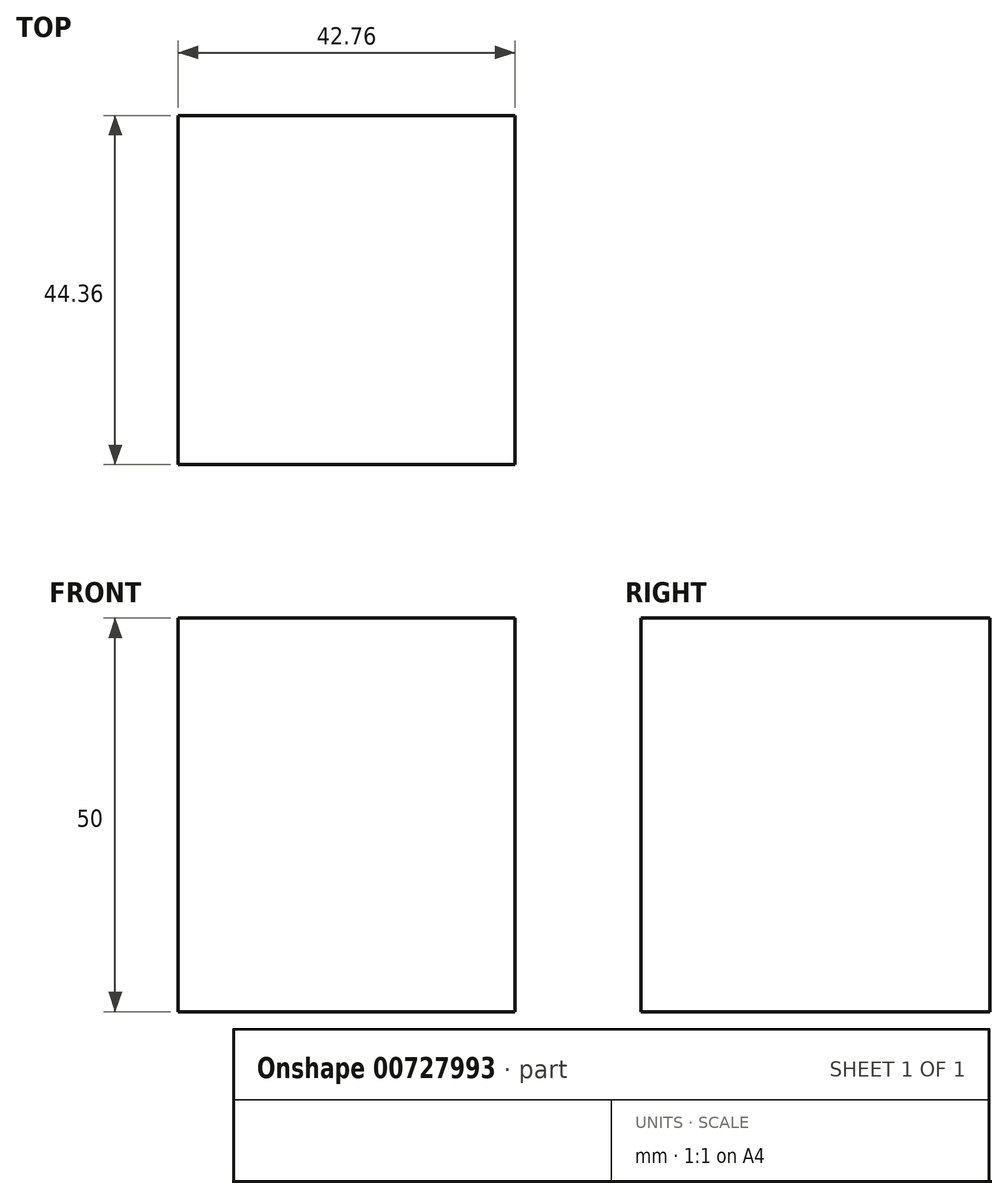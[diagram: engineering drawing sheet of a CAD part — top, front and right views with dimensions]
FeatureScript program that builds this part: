
annotation { "Feature Type Name" : "Feature", "Feature Type Description" : "" }
export const myFeature = defineFeature(function(context is Context, id is Id, definition is map)
    precondition{}
    {
        {
            var Q0;
            Q0=qCreatedBy(makeId("Top.planeOp"),FACE);
            var sketch = newSketch(context, id + "F0", { "sketchPlane" : qUnion([Q0])});
            skLineSegment(sketch, "E0.bottom", {"start": v(15.4, -28.48) * mm, "end": v(-27.36, -28.48) * mm});
            skLineSegment(sketch, "E0.top", {"start": v(15.4, 15.88) * mm, "end": v(-27.36, 15.88) * mm});
            skLineSegment(sketch, "E0.left", {"start": v(15.4, -28.48) * mm, "end": v(15.4, 15.88) * mm});
            skLineSegment(sketch, "E0.right", {"start": v(-27.36, -28.48) * mm, "end": v(-27.36, 15.88) * mm});
            skSolve(sketch);
        }
        {
            var Q0;
            Q0 = qSketchRegion(id + "F0", true);
            extrude(context, id + "F1", {"entities" : qUnion([Q0]), "depth" : 50 * mm, "offsetDistance" : 25.4 * mm});
        }
        {
            var Q0;
            Q0=makeQuery(id+"F1.opExtrude","CAP_FACE",FACE,{"disambiguationData":[OSD([sQuery(id+"F0.wireOp",EDGE,"E0.bottom"),sQuery(id+"F0.wireOp",EDGE,"E0.top"),sQuery(id+"F0.wireOp",EDGE,"E0.left"),sQuery(id+"F0.wireOp",EDGE,"E0.right")])],"isStart":false});
            var sketch = newSketch(context, id + "F2", { "sketchPlane" : qUnion([Q0])});
            skCircle(sketch, "E1", {"center": v(-3.33, -6.3) * mm, "radius": 13.52 * mm});
            skPoint(sketch, "E1.centerSnap0", {"position": v(15.4, -6.3) * mm});
            skCircle(sketch, "E2", {"center": v(-2.76, 7.2) * mm, "radius": 8.93 * mm});
            skSolve(sketch);
        }
        {
            var Q0;
            Q0=sQuery(id+"F2.wireOp",EDGE,"E1");
            extrude(context, id + "F3", {"bodyType" : ToolBodyType.SURFACE, "surfaceEntities" : qUnion([Q0]), "depth" : 50 * mm, "offsetDistance" : 25.4 * mm});
        }
    });
